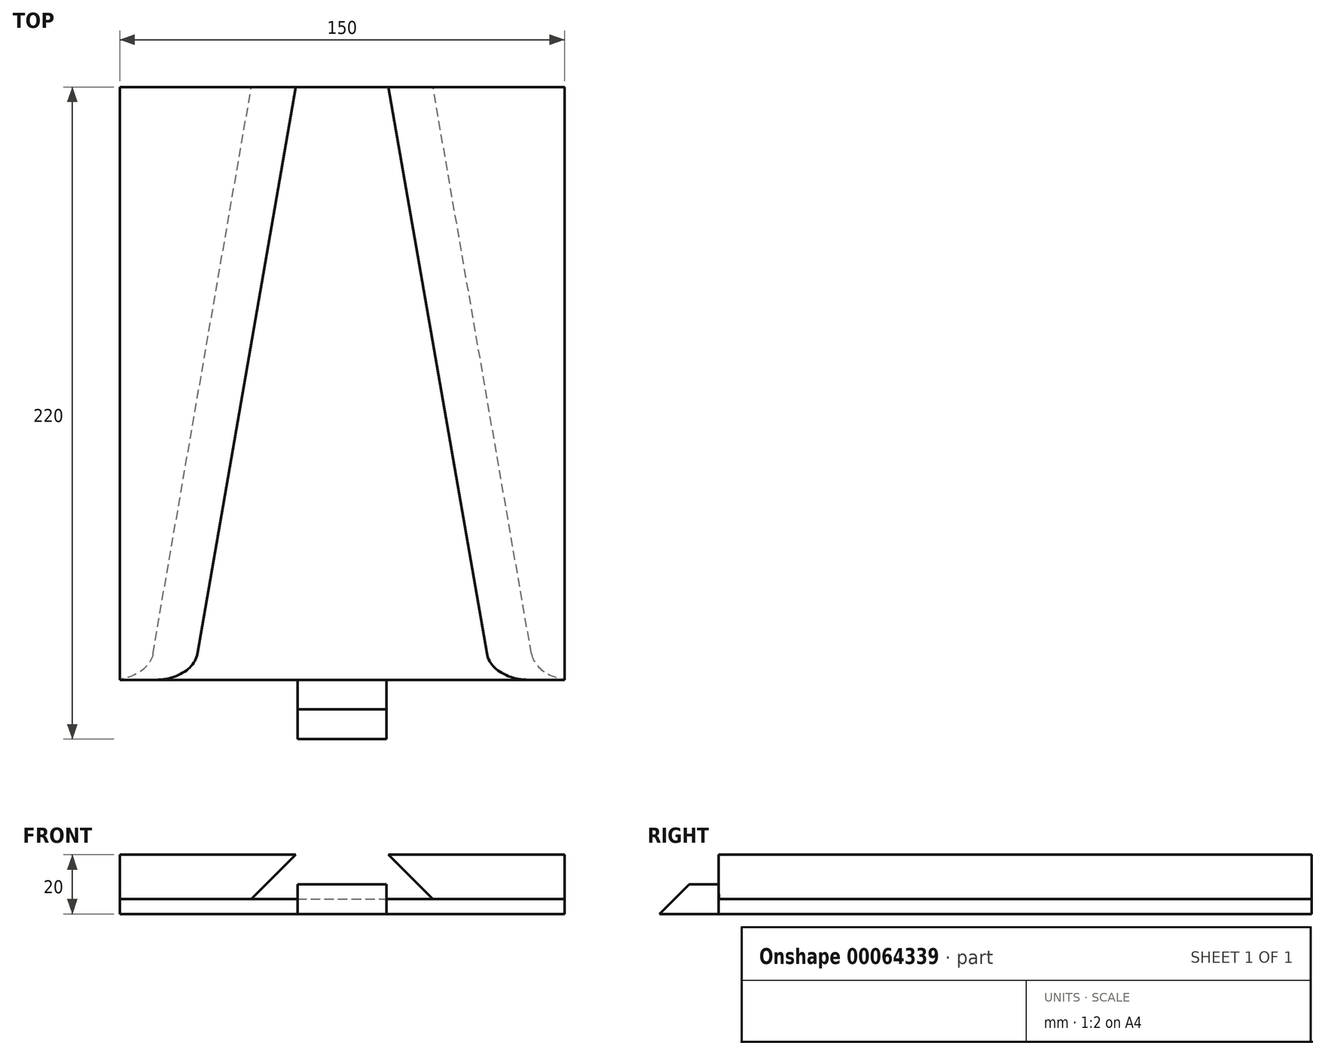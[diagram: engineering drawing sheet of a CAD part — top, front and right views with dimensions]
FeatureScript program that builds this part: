
annotation { "Feature Type Name" : "Feature", "Feature Type Description" : "" }
export const myFeature = defineFeature(function(context is Context, id is Id, definition is map)
    precondition{}
    {
        {
            var Q0;
            Q0=qCreatedBy(makeId("Front.planeOp"),FACE);
            var sketch = newSketch(context, id + "F0", { "sketchPlane" : qUnion([Q0])});
            skLineSegment(sketch, "E0", {"start": v(0, 0) * mm, "end": v(0, 15) * mm});
            skLineSegment(sketch, "E1", {"start": v(0, 15) * mm, "end": v(-60, 15) * mm});
            skLineSegment(sketch, "E2", {"start": v(-60, 15) * mm, "end": v(-52.5, 7.5) * mm});
            skLineSegment(sketch, "E3", {"start": v(-45, 0) * mm, "end": v(0, 0) * mm});
            skLineSegment(sketch, "E4", {"start": v(-52.5, 7.5) * mm, "end": v(-45, 0) * mm});
            skPoint(sketch, "E5.start.orphan", {"position": v(-40, 0) * mm});
            skSolve(sketch);
        }
        {
            var Q0;
            Q0=makeQuery(id+"F0.imprint","IMPRINT",FACE,{"disambiguationData":[TD([[makeQuery(id+"F0.imprint","IMPRINT",EDGE,{"derivedFrom":sQuery(id+"F0.wireOp",EDGE,"E0")}),1.0]])]});
            extrude(context, id + "F1", {"entities" : qUnion([Q0]), "depth" : 200 * mm});
        }
        {
            var Q0;
            Q0=makeQuery(id+"F1.opExtrude","CAP_EDGE",EDGE,{"disambiguationData":[OSD([sQuery(id+"F0.wireOp",EDGE,"E2")])],"isStart":false});
            var Q1;
            Q1=makeQuery(id+"F1.opExtrude","CAP_EDGE",EDGE,{"disambiguationData":[OSD([sQuery(id+"F0.wireOp",EDGE,"CI5bpjFa-Tzdc-Pcp4-TJj9-QjqtSVukENM3")])],"isStart":false});
            chamfer(context, id + "F2", {"entities" : qUnion([Q0, Q1]), "chamferType" : ChamferType.OFFSET_ANGLE, "width" : 25 * mm, "oppositeDirection" : false, "angle" : 83 * degree, "tangentPropagation" : true});
        }
        {
            var Q0;
            {var subQ0=sQuery(id+"F0.wireOp",EDGE,"E2");Q0=makeQuery(id+"F2.opChamfer","BLEND_EDGE",EDGE,{"blendedFrom":[makeQuery(id+"F1.opExtrude","CAP_EDGE",EDGE,{"disambiguationData":[OSD([subQ0])],"isStart":false}),makeQuery(id+"F1.opExtrude","CAP_FACE",FACE,{"disambiguationData":[OSD([sQuery(id+"F0.wireOp",EDGE,"E0"),sQuery(id+"F0.wireOp",EDGE,"E1"),subQ0,sQuery(id+"F0.wireOp",EDGE,"E3")])],"isStart":false})],"blendedInto":[makeQuery(id+"F1.opExtrude","CAP_FACE",FACE,{"disambiguationData":[OSD([sQuery(id+"F0.wireOp",EDGE,"E0"),sQuery(id+"F0.wireOp",EDGE,"E1"),subQ0,sQuery(id+"F0.wireOp",EDGE,"E3")])],"isStart":false})]});}
            var Q1;
            {var subQ0=sQuery(id+"F0.wireOp",EDGE,"CI5bpjFa-Tzdc-Pcp4-TJj9-QjqtSVukENM3");Q1=makeQuery(id+"F2.opChamfer","BLEND_EDGE",EDGE,{"blendedFrom":[makeQuery(id+"F1.opExtrude","CAP_EDGE",EDGE,{"disambiguationData":[OSD([subQ0])],"isStart":false}),makeQuery(id+"F1.opExtrude","CAP_FACE",FACE,{"disambiguationData":[OSD([sQuery(id+"F0.wireOp",EDGE,"E0"),sQuery(id+"F0.wireOp",EDGE,"E1"),sQuery(id+"F0.wireOp",EDGE,"E2"),sQuery(id+"F0.wireOp",EDGE,"E3"),subQ0,sQuery(id+"F0.wireOp",EDGE,"E5")])],"isStart":false})],"blendedInto":[makeQuery(id+"F1.opExtrude","CAP_FACE",FACE,{"disambiguationData":[OSD([sQuery(id+"F0.wireOp",EDGE,"E0"),sQuery(id+"F0.wireOp",EDGE,"E1"),sQuery(id+"F0.wireOp",EDGE,"E2"),sQuery(id+"F0.wireOp",EDGE,"E3"),subQ0,sQuery(id+"F0.wireOp",EDGE,"E5")])],"isStart":false})]});}
            fillet(context, id + "F3", {"entities" : qUnion([Q0, Q1]), "radius" : 10 * mm, "tangentPropagation" : true, "allowEdgeOverflow" : false});
        }
        {
            var Q0;
            Q0=qCreatedBy(makeId("Front.planeOp"),FACE);
            var sketch = newSketch(context, id + "F4", { "sketchPlane" : qUnion([Q0])});
            skLineSegment(sketch, "E6", {"start": v(0, 0) * mm, "end": v(0, -5) * mm});
            skLineSegment(sketch, "E7", {"start": v(0, -5) * mm, "end": v(-150, -5) * mm});
            skLineSegment(sketch, "E8", {"start": v(-150, -5) * mm, "end": v(-150, 0) * mm});
            skLineSegment(sketch, "E9", {"start": v(-150, 0) * mm, "end": v(0, 0) * mm});
            skSolve(sketch);
        }
        {
            var Q0;
            Q0=makeQuery(id+"F4.imprint","IMPRINT",FACE,{"disambiguationData":[TD([[makeQuery(id+"F4.imprint","IMPRINT",EDGE,{"derivedFrom":sQuery(id+"F4.wireOp",EDGE,"E6")}),-1.0]])]});
            extrude(context, id + "F5", {"entities" : qUnion([Q0]), "depth" : 200 * mm});
        }
        {
            var Q0;
            Q0=qCreatedBy(makeId("Right.planeOp"),FACE);
            cPlane(context, id + "F6", {"entities" : qUnion([Q0]), "cplaneType" : CPlaneType.OFFSET, "offset" : 75 * mm, "oppositeDirection" : true, "width" : 150 * mm, "height" : 150 * mm});
        }
        {
            var Q0;
            Q0=makeQuery(id+"F1.opExtrude","SWEPT_BODY",BODY,{"disambiguationData":[OSD([sQuery(id+"F0.wireOp",EDGE,"E0"),sQuery(id+"F0.wireOp",EDGE,"E1"),sQuery(id+"F0.wireOp",EDGE,"E2"),sQuery(id+"F0.wireOp",EDGE,"E3"),sQuery(id+"F0.wireOp",EDGE,"E4")])]});
            var Q1;
            Q1=qCreatedBy(id+"F6.planeOp",FACE);
            mirror(context, id + "F7", {"entities" : qUnion([Q0]), "mirrorPlane" : qUnion([Q1])});
        }
        {
            var Q0;
            Q0=makeQuery(id+"F5.opExtrude","CAP_FACE",FACE,{"disambiguationData":[OSD([sQuery(id+"F4.wireOp",EDGE,"E6"),sQuery(id+"F4.wireOp",EDGE,"E7"),sQuery(id+"F4.wireOp",EDGE,"E8"),sQuery(id+"F4.wireOp",EDGE,"E9")])],"isStart":false});
            var sketch = newSketch(context, id + "F8", { "sketchPlane" : qUnion([Q0])});
            skLineSegment(sketch, "E10.rect.bottom", {"start": v(-60, -5) * mm, "end": v(-90, -5) * mm});
            skLineSegment(sketch, "E10.rect.top", {"start": v(-60, 5) * mm, "end": v(-90, 5) * mm});
            skLineSegment(sketch, "E10.rect.left", {"start": v(-60, -5) * mm, "end": v(-60, 5) * mm});
            skLineSegment(sketch, "E10.rect.right", {"start": v(-90, -5) * mm, "end": v(-90, 5) * mm});
            skPoint(sketch, "E10.rect.middle", {"position": v(-75, 0) * mm});
            skSolve(sketch);
        }
        {
            var Q0;
            {var subQ0=sQuery(id+"F8.wireOp",EDGE,"E10.rect.bottom");Q0=makeQuery(id+"F8.imprint","IMPRINT",FACE,{"disambiguationData":[TD([[makeQuery(id+"F8.imprint","IMPRINT",EDGE,{"derivedFrom":subQ0}),-1.0]])]});}
            var Q1;
            {var subQ0=sQuery(id+"F8.wireOp",EDGE,"E10.rect.top");Q1=makeQuery(id+"F8.imprint","IMPRINT",FACE,{"disambiguationData":[TD([[makeQuery(id+"F8.imprint","IMPRINT",EDGE,{"derivedFrom":subQ0}),1.0]])]});}
            extrude(context, id + "F9", {"entities" : qUnion([Q0, Q1]), "operationType" : NewBodyOperationType.ADD, "depth" : 25 * mm});
        }
        {
            var Q0;
            Q0=makeQuery(id+"F9.opExtrude","CAP_EDGE",EDGE,{"disambiguationData":[OSD([sQuery(id+"F8.wireOp",EDGE,"E10.rect.top")])],"isStart":false});
            chamfer(context, id + "F10", {"entities" : qUnion([Q0]), "width" : 15 * mm, "tangentPropagation" : true});
        }
    });
